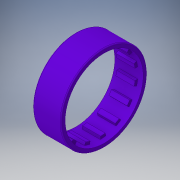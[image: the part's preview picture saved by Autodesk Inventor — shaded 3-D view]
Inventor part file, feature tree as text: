
AUTODESK INVENTOR PART (.ipt)
format: ipt  version: 2018 (Build 220112000, 112)  size: 229,376 bytes
history: native  units: in
note: dims shown in document units (in); Inventor stores cm internally (conversion verified against a paired STEP export)
features: sketch x4, revolve x2, extrude x2, pattern_circular x1, projected_geometry x1
ambient origin geometry x8: Origin, YZ Plane, XZ Plane, XY Plane, X Axis, Y Axis, Z Axis, Center Point
bodies: Solid1 (feature_tree)
feature tree (10):
  revolve  "Revolution1"  [1 undecoded]
  revolve  "Revolution2"  [1 undecoded]
  extrude  "Extrusion1"  Depth=0.1in
  extrude  "Extrusion2"  TaperAngle=90.0deg  [1 undecoded]
  pattern_circular  "Circular Pattern1"  [2 undecoded]
  sketch  "Sketch1"  dims[d0=0.772in d1=0.56in]
  sketch  "Sketch2"  dims[d2=0.08in d3=0.02in]
  projected_geometry  "Projected Loop1"
  sketch  "Sketch3"  dims[d4=90.0deg d5=0.1in]
  sketch  "Sketch4"  dims[d6=0.1in d7=90.0deg d8=1.435in d9=1.0in d10=0.0in d13=1.0in d14=0.0in d15=5.9055in d16=360.0deg]
note: 5 required parameter values undecoded (feature->parameter linkage not recoverable at this tier; creation-order binding heuristic only, values carry confidence <= 0.55)